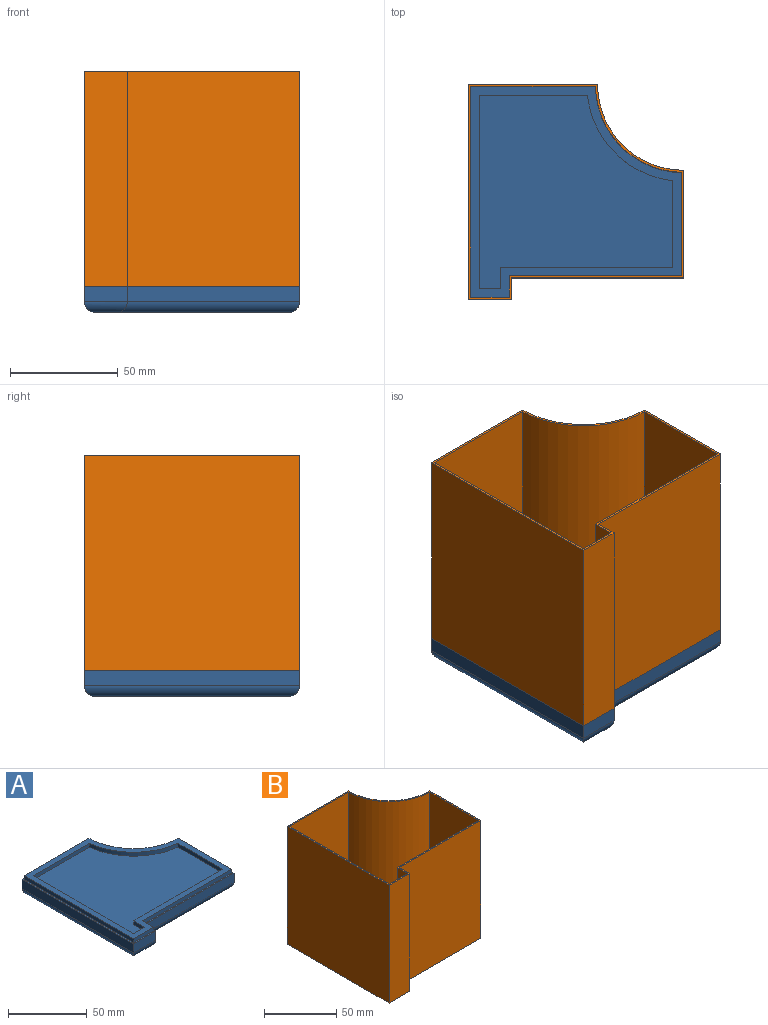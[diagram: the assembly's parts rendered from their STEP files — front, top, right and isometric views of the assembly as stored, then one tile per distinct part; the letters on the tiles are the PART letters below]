
ASSEMBLY  parts=2 mates=1
PART A: 32 faces, bbox 100x100x15 mm
  f0: plane 98x98mm, normal (0,0,1), area 1431.1mm2, adj f1,f2,f3,f4,f5,f6,f7,f9
  f1: plane 40.28x3mm, normal (-1,0,0), area 120.8mm2, adj f0,f2,f7,f8
  f2: cylinder r=45mm len=39.72mm, axis (0,0,1), area 182mm2, adj f0,f1,f3,f8
  f3: plane 50.28x3mm, normal (0,-1,0), area 150.8mm2, adj f0,f2,f4,f8
  f4: plane 90x3mm, normal (1,0,0), area 270mm2, adj f0,f3,f5,f8
  f5: plane 10x3mm, normal (0,1,0), area 30mm2, adj f0,f4,f6,f8
  f6: plane 10x3mm, normal (-1,0,0), area 30mm2, adj f0,f5,f7,f8
  f7: plane 80x3mm, normal (0,1,0), area 240mm2, adj f0,f1,f6,f8
  f8: plane 90x90mm, normal (0,0,1), area 6133.6mm2, adj f1,f2,f3,f4,f5,f6,f7
  f9: plane 48.01x3mm, normal (1,0,0), area 144mm2, adj f0,f10,f15,f16
  f10: plane 80x3mm, normal (0,-1,0), area 240mm2, adj f0,f9,f11,f16
  f11: plane 10x3mm, normal (1,0,0), area 30mm2, adj f0,f10,f12,f16
  f12: plane 18x3mm, normal (0,-1,0), area 54mm2, adj f0,f11,f13,f16
  f13: plane 98x3mm, normal (-1,0,0), area 294mm2, adj f0,f12,f14,f16
  f14: plane 58.01x3mm, normal (0,1,0), area 174mm2, adj f0,f13,f15,f16
  f15: cylinder r=41mm len=39.99mm, axis (0,0,1), area 187.2mm2, adj f0,f9,f14,f16
  f16: plane 100x100mm, normal (0,0,1), area 378.6mm2, adj f9,f10,f11,f12,f13,f14,f15,f18
  f17: plane 90x90mm, normal (0,0,-1), area 6133.6mm2, adj f25,f26,f27,f28,f29,f30,f31
  f18: plane 10x7mm, normal (1,0,0), area 70mm2, adj f16,f19,f20,f29
  f19: plane 80x7mm, normal (0,-1,0), area 560mm2, adj f16,f18,f24,f27
  f20: plane 20x7mm, normal (0,-1,0), area 140mm2, adj f16,f18,f21,f31
  f21: plane 100x7mm, normal (-1,0,0), area 700mm2, adj f16,f20,f22,f30
  f22: plane 60x7mm, normal (0,1,0), area 420mm2, adj f16,f21,f23,f28
  f23: cylinder r=40mm len=40mm, axis (0,0,-1), area 439.8mm2, adj f16,f22,f24,f26
  f24: plane 50x7mm, normal (1,0,0), area 350mm2, adj f16,f19,f23,f25
  f25: cylinder r=5mm len=50mm, axis (0,1,0), area 364.7mm2, adj f17,f24,f26,f27
  f26: torus R=45mm, axis (0,0,1), area 487.3mm2, adj f17,f23,f25,f28
  f27: cylinder r=5mm len=85mm, axis (1,0,0), area 628.3mm2, adj f17,f19,f25,f29
  f28: cylinder r=5mm len=60mm, axis (-1,0,0), area 443.2mm2, adj f17,f22,f26,f30
  f29: cylinder r=5mm len=15mm, axis (0,1,0), area 78.5mm2, adj f17,f18,f27,f31
  f30: cylinder r=5mm len=100mm, axis (0,-1,0), area 756.9mm2, adj f17,f21,f28,f31
  f31: cylinder r=5mm len=20mm, axis (1,0,0), area 128.5mm2, adj f17,f20,f29,f30
PART B: 16 faces, bbox 100x100x100 mm
  f0: cylinder r=41mm len=100mm, axis (0,0,-1), area 6240.2mm2, adj f1,f13,f14,f15
  f1: plane 100x48.01mm, normal (-1,0,0), area 4801.2mm2, adj f0,f2,f14,f15
  f2: plane 100x80mm, normal (0,1,0), area 8000mm2, adj f1,f3,f14,f15
  f3: plane 100x10mm, normal (-1,0,0), area 1000mm2, adj f2,f4,f14,f15
  f4: plane 100x18mm, normal (0,1,0), area 1800mm2, adj f3,f5,f14,f15
  f5: plane 100x98mm, normal (1,0,0), area 9800mm2, adj f4,f13,f14,f15
  f6: plane 100x80mm, normal (0,-1,0), area 8000mm2, adj f7,f12,f14,f15
  f7: plane 100x50mm, normal (1,0,0), area 5000mm2, adj f6,f8,f14,f15
  f8: cylinder r=40mm len=100mm, axis (0,0,-1), area 6283.2mm2, adj f7,f9,f14,f15
  f9: plane 100x60mm, normal (0,1,0), area 6000mm2, adj f8,f10,f14,f15
  f10: plane 100x100mm, normal (-1,0,0), area 10000mm2, adj f9,f11,f14,f15
  f11: plane 100x20mm, normal (0,-1,0), area 2000mm2, adj f10,f12,f14,f15
  f12: plane 100x10mm, normal (1,0,0), area 1000mm2, adj f6,f11,f14,f15
  f13: plane 100x58.01mm, normal (0,-1,0), area 5801.2mm2, adj f0,f5,f14,f15
  f14: plane 100x100mm, normal (0,0,1), area 378.6mm2, adj f0,f1,f2,f3,f4,f5,f6,f7
  f15: plane 100x100mm, normal (0,0,-1), area 378.6mm2, adj f0,f1,f2,f3,f4,f5,f6,f7
PLACE A t=(44.15,10.1,33.35)mm
PLACE B t=(44.15,10.1,33.35)mm
MATE fastened A.f16 <-> B.f15  axis (0,0,1) through (44.15,-39.9,45.35)mm
